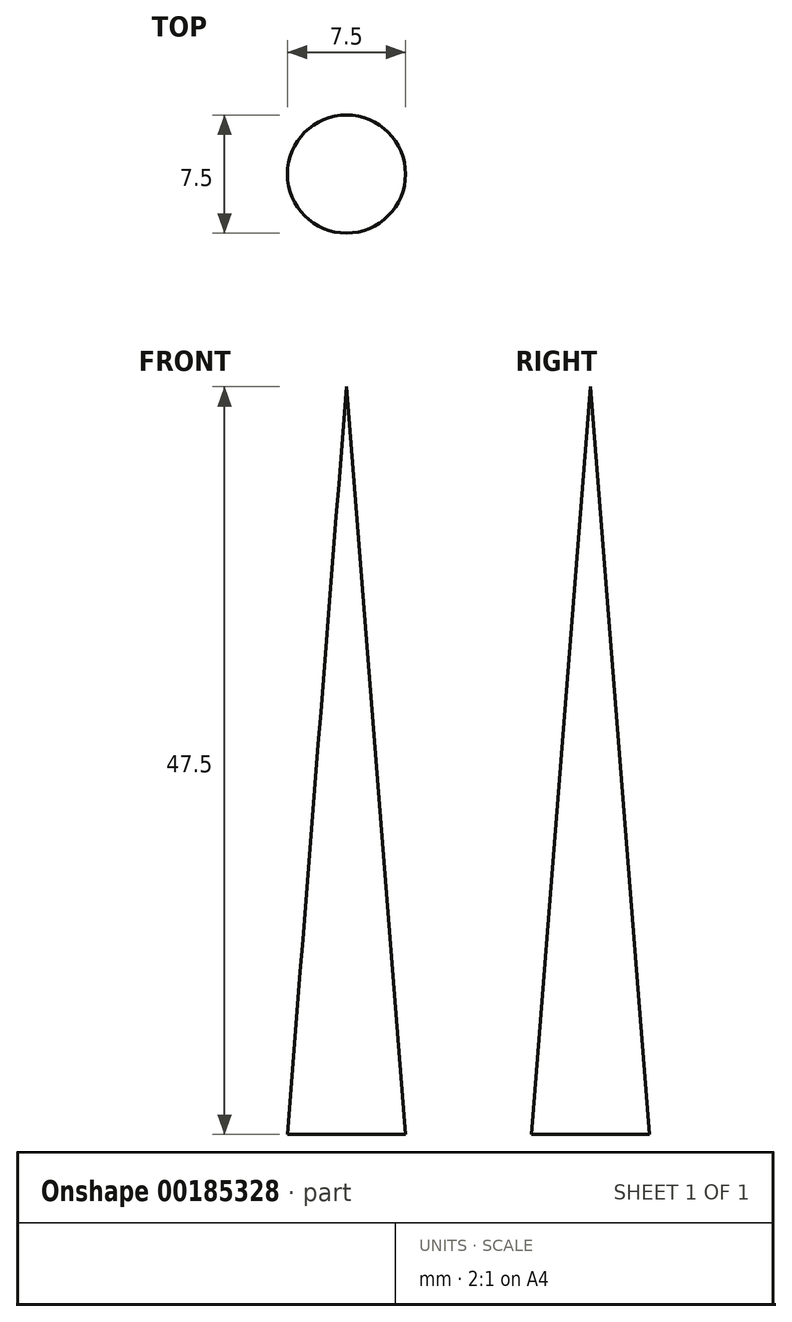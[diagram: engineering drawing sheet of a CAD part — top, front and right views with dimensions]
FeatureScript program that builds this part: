
annotation { "Feature Type Name" : "Feature", "Feature Type Description" : "" }
export const myFeature = defineFeature(function(context is Context, id is Id, definition is map)
    precondition{}
    {
        {
            var Q0;
            Q0=qCreatedBy(makeId("Front.planeOp"),FACE);
            var sketch = newSketch(context, id + "F0", { "sketchPlane" : qUnion([Q0])});
            skLineSegment(sketch, "E0", {"start": v(0, 0) * mm, "end": v(-3.75, 0) * mm});
            skLineSegment(sketch, "E1", {"start": v(-3.75, 0) * mm, "end": v(0, 47.5) * mm});
            skLineSegment(sketch, "E2", {"start": v(0, 47.5) * mm, "end": v(0, 0) * mm});
            skSolve(sketch);
        }
        {
            var Q0;
            Q0=makeQuery(id+"F0.imprint","IMPRINT",FACE,{"disambiguationData":[TD([[makeQuery(id+"F0.imprint","IMPRINT",EDGE,{"derivedFrom":sQuery(id+"F0.wireOp",EDGE,"E0")}),-1.0]])]});
            var Q1;
            Q1=sQuery(id+"F0.wireOp",EDGE,"E2");
            revolve(context, id + "F1", {"entities" : qUnion([Q0]), "axis" : qUnion([Q1]), "revolveType" : RevolveType.FULL});
        }
    });
